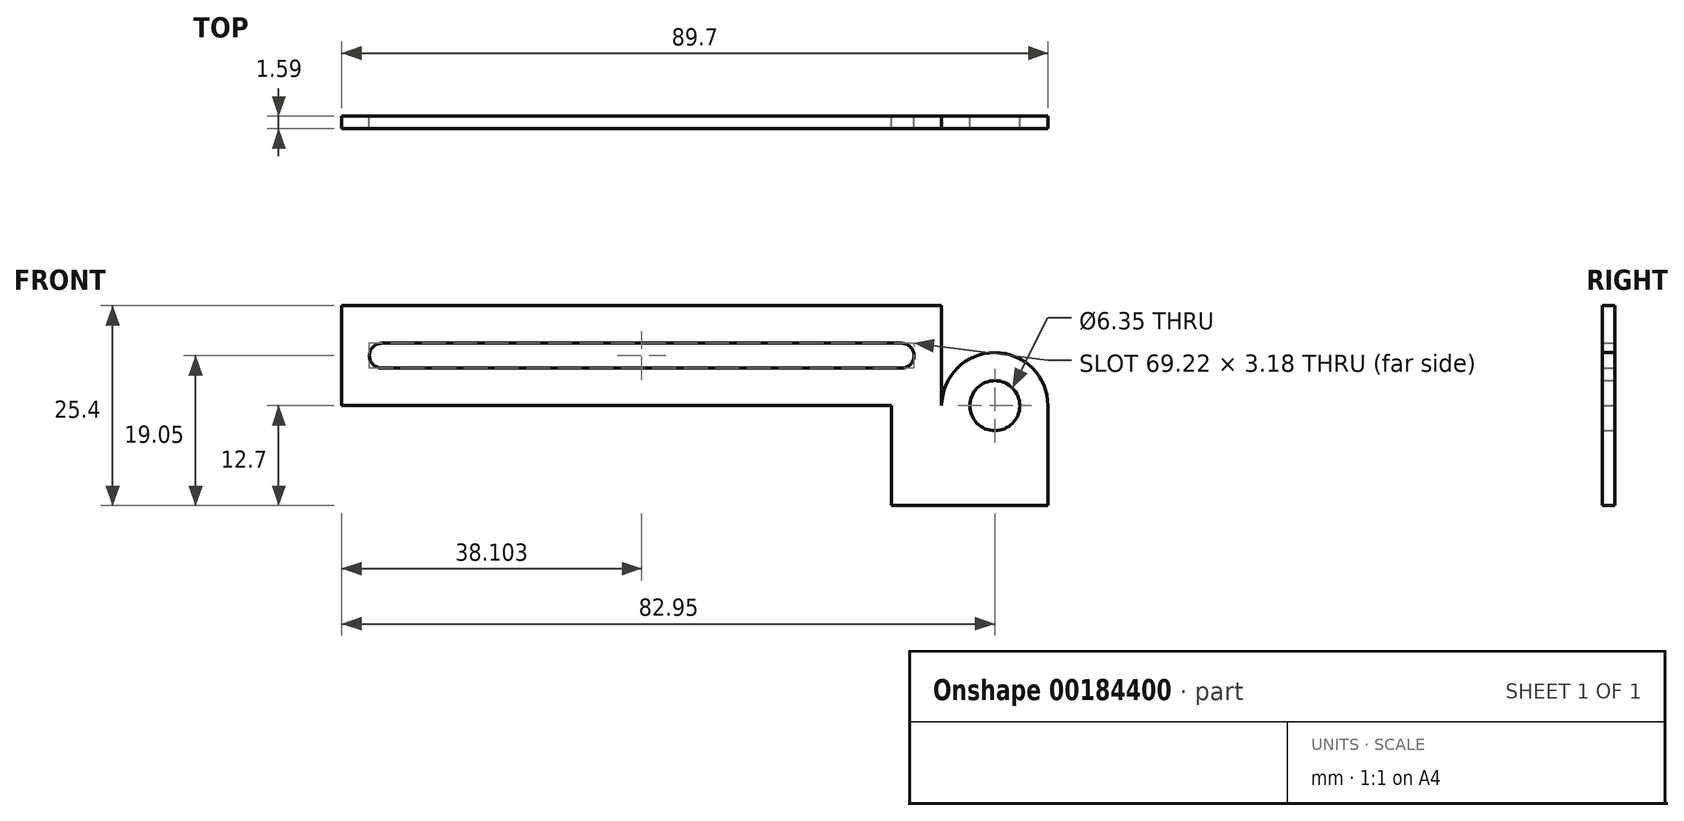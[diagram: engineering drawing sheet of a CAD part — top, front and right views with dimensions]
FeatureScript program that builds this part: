
annotation { "Feature Type Name" : "Feature", "Feature Type Description" : "" }
export const myFeature = defineFeature(function(context is Context, id is Id, definition is map)
    precondition{}
    {
        {
            var Q0;
            Q0=qCreatedBy(makeId("Front.planeOp"),FACE);
            var sketch = newSketch(context, id + "F0", { "sketchPlane" : qUnion([Q0])});
            skLineSegment(sketch, "E0.right", {"start": v(6.75, 0) * mm, "end": v(6.75, 12.7) * mm});
            skLineSegment(sketch, "E1", {"start": v(-82.95, 12.7) * mm, "end": v(-82.95, 25.4) * mm});
            skLineSegment(sketch, "E2", {"start": v(-82.95, 25.4) * mm, "end": v(-6.75, 25.4) * mm});
            skLineSegment(sketch, "E3", {"start": v(-6.75, 25.4) * mm, "end": v(-6.75, 12.7) * mm});
            skLineSegment(sketch, "E4", {"start": v(6.75, 0) * mm, "end": v(-13.1, 0) * mm});
            skLineSegment(sketch, "E5", {"start": v(-13.1, 0) * mm, "end": v(-13.1, 12.7) * mm});
            skLineSegment(sketch, "E6", {"start": v(-13.1, 12.7) * mm, "end": v(-82.95, 12.7) * mm});
            skArc(sketch, "E7", {"start": v(6.75, 12.7) * mm, "mid": v(0, 19.45) * mm, "end": v(-6.75, 12.7) * mm});
            skCircle(sketch, "E8", {"center": v(0, 12.7) * mm, "radius": 3.18 * mm});
            skLineSegment(sketch, "E9.bottom", {"start": v(-77.87, 20.64) * mm, "end": v(-11.83, 20.64) * mm});
            skLineSegment(sketch, "E9.top", {"start": v(-77.87, 17.46) * mm, "end": v(-11.83, 17.46) * mm});
            skArc(sketch, "E10", {"start": v(-11.83, 17.46) * mm, "mid": v(-10.24, 19.05) * mm, "end": v(-11.83, 20.64) * mm});
            skArc(sketch, "E11", {"start": v(-77.87, 20.64) * mm, "mid": v(-79.45, 19.05) * mm, "end": v(-77.87, 17.46) * mm});
            skSolve(sketch);
        }
        {
            var Q0;
            Q0 = qSketchRegion(id + "F0", true);
            extrude(context, id + "F1", {"entities" : qUnion([Q0]), "depth" : 1.59 * mm});
        }
    });
